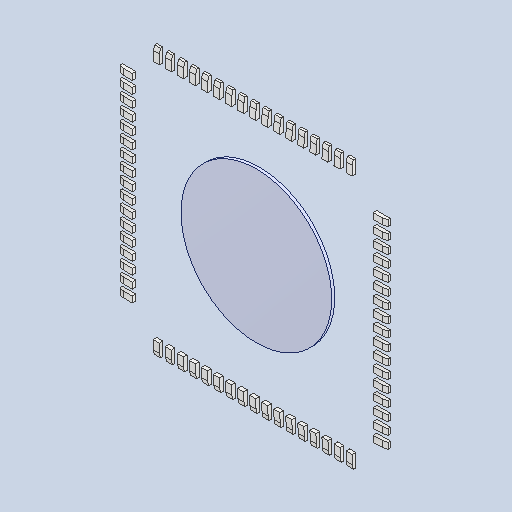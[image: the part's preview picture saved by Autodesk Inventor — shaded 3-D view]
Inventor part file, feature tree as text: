
AUTODESK INVENTOR PART (.ipt)
format: ipt  version: 2022 (Build 260153000, 153)  size: 411,136 bytes
history: mixed  units: in
note: dims shown in document units (in); Inventor stores cm internally (conversion verified against a paired STEP export)
features: fillet x1, other x1, imported_body x1
bodies: Solid25 (imported_parasolid), Solid26 (imported_parasolid), Solid27 (imported_parasolid), Solid28 (imported_parasolid), Solid29 (imported_parasolid), Solid30 (imported_parasolid), Solid31 (imported_parasolid), Solid32 (imported_parasolid), Solid33 (imported_parasolid), Solid34 (imported_parasolid), Solid35 (imported_parasolid), Solid36 (imported_parasolid), Solid37 (imported_parasolid), Solid38 (imported_parasolid), Solid39 (imported_parasolid), Solid40 (imported_parasolid), Solid41 (imported_parasolid), Solid42 (imported_parasolid), Solid43 (imported_parasolid), Solid44 (imported_parasolid), Solid45 (imported_parasolid), Solid46 (imported_parasolid), Solid47 (imported_parasolid), Solid48 (imported_parasolid), Solid49 (imported_parasolid), Solid50 (imported_parasolid), Solid51 (imported_parasolid), Solid52 (imported_parasolid), Solid53 (imported_parasolid), Solid54 (imported_parasolid), Solid55 (imported_parasolid), Solid56 (imported_parasolid), Solid57 (imported_parasolid), Solid58 (imported_parasolid), Solid59 (imported_parasolid), Solid60 (imported_parasolid), Solid61 (imported_parasolid), Solid62 (imported_parasolid), Solid63 (imported_parasolid), Solid64 (imported_parasolid), Solid65 (imported_parasolid), Solid66 (imported_parasolid), Solid67 (imported_parasolid), Solid68 (imported_parasolid), Solid69 (imported_parasolid), Solid70 (imported_parasolid)
feature tree (3):
  fillet  "Fillet1"  [1 undecoded]
  other  "Cut-Extrude2"
  imported_body  NMx_Import_Brep_tag  [imported B-rep: ~489 faces, bbox_mm=[8.9, 8.9, 0.9]]
note: 1 required parameter value undecoded (feature->parameter linkage not recoverable at this tier; creation-order binding heuristic only, values carry confidence <= 0.55)
